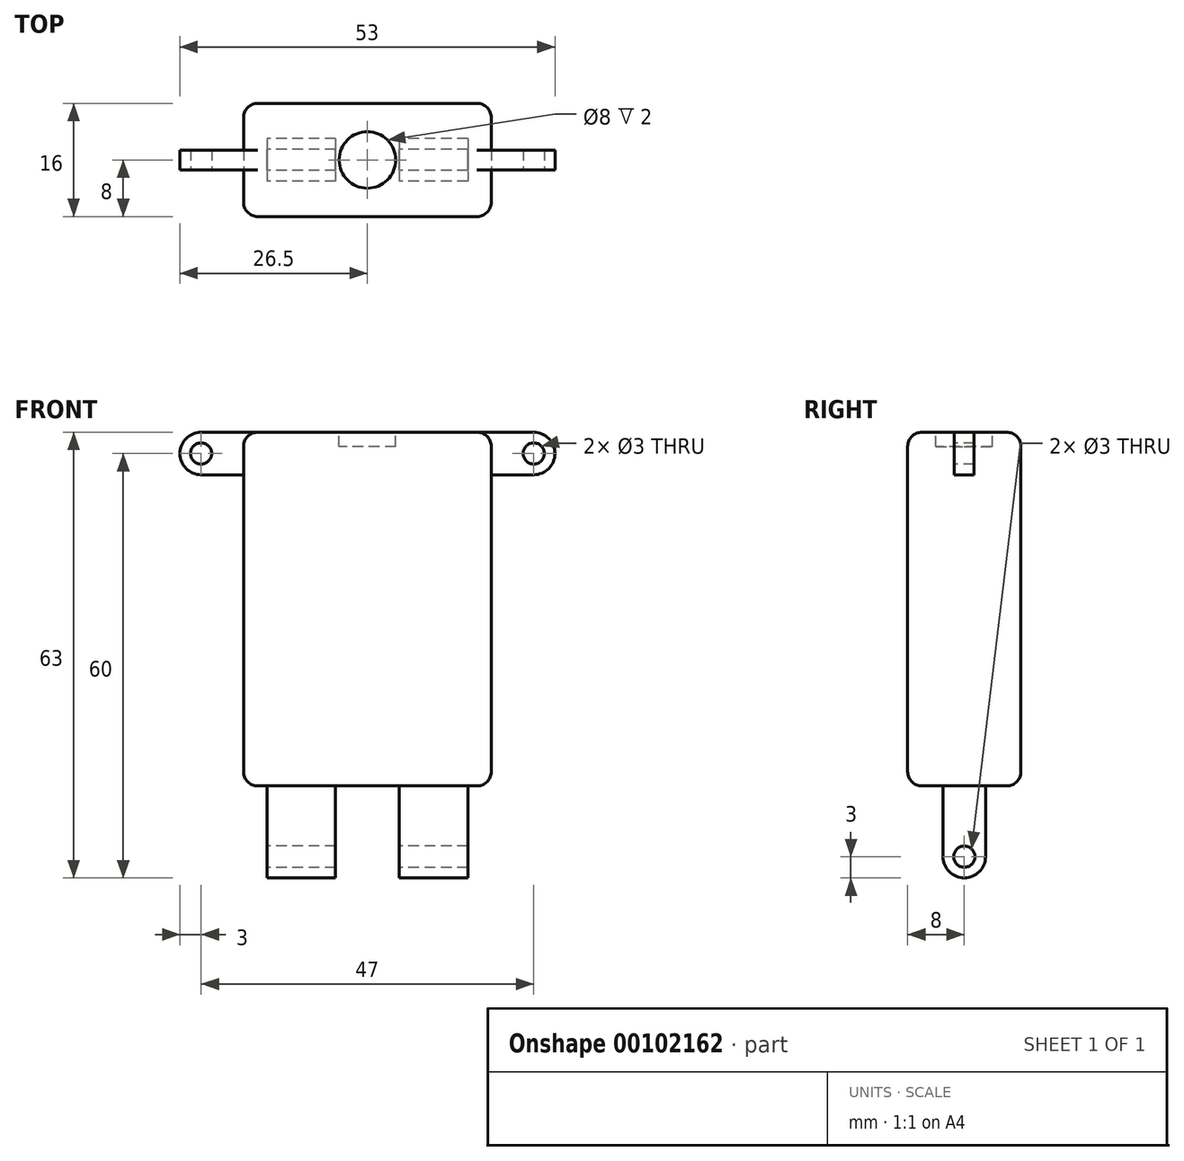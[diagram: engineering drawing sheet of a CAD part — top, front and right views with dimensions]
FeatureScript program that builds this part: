
annotation { "Feature Type Name" : "Feature", "Feature Type Description" : "" }
export const myFeature = defineFeature(function(context is Context, id is Id, definition is map)
    precondition{}
    {
        {
            var Q0;
            Q0=qCreatedBy(makeId("Right.planeOp"),FACE);
            var sketch = newSketch(context, id + "F0", { "sketchPlane" : qUnion([Q0])});
            skLineSegment(sketch, "E0.bottom", {"start": v(8, 0) * mm, "end": v(-8, 0) * mm});
            skLineSegment(sketch, "E0.top", {"start": v(8, 50) * mm, "end": v(-8, 50) * mm});
            skLineSegment(sketch, "E0.left", {"start": v(8, 0) * mm, "end": v(8, 50) * mm});
            skLineSegment(sketch, "E0.right", {"start": v(-8, 0) * mm, "end": v(-8, 50) * mm});
            skLineSegment(sketch, "E1.bottom", {"start": v(-3, 0) * mm, "end": v(3, 0) * mm});
            skLineSegment(sketch, "E1.top", {"start": v(-1.5, -10) * mm, "end": v(1.5, -10) * mm});
            skLineSegment(sketch, "E1.left", {"start": v(-3, 0) * mm, "end": v(-3, -10) * mm});
            skLineSegment(sketch, "E1.right", {"start": v(3, 0) * mm, "end": v(3, -10) * mm});
            skCircle(sketch, "E2", {"center": v(0, -10) * mm, "radius": 3 * mm});
            skCircle(sketch, "E3", {"center": v(0, -10) * mm, "radius": 1.5 * mm});
            skSolve(sketch);
        }
        {
            var Q0;
            Q0 = qSketchRegion(id + "F0", true);
            extrude(context, id + "F1", {"entities" : qUnion([Q0]), "depth" : 35 * mm, "symmetric" : true});
        }
        {
            var Q0;
            Q0=qCreatedBy(makeId("Front.planeOp"),FACE);
            var sketch = newSketch(context, id + "F2", { "sketchPlane" : qUnion([Q0])});
            skLineSegment(sketch, "E4.bottom", {"start": v(-14.2, 0) * mm, "end": v(-4.5, 0) * mm, "construction": true});
            skLineSegment(sketch, "E4.top", {"start": v(-14.2, -15) * mm, "end": v(-4.5, -15) * mm, "construction": true});
            skLineSegment(sketch, "E4.left", {"start": v(-14.2, 0) * mm, "end": v(-14.2, -15) * mm, "construction": true});
            skLineSegment(sketch, "E4.right", {"start": v(-4.5, 0) * mm, "end": v(-4.5, -15) * mm, "construction": true});
            skLineSegment(sketch, "E5.bottom", {"start": v(-14.2, 0) * mm, "end": v(-20.57, 0) * mm});
            skLineSegment(sketch, "E5.top", {"start": v(-14.2, -17.87) * mm, "end": v(-20.57, -17.87) * mm});
            skLineSegment(sketch, "E5.left", {"start": v(-14.2, 0) * mm, "end": v(-14.2, -17.87) * mm});
            skLineSegment(sketch, "E5.right", {"start": v(-20.57, 0) * mm, "end": v(-20.57, -17.87) * mm});
            skLineSegment(sketch, "E6.bottom", {"start": v(-4.5, 0) * mm, "end": v(0, 0) * mm});
            skLineSegment(sketch, "E6.top", {"start": v(-4.5, -17.87) * mm, "end": v(0, -17.87) * mm});
            skLineSegment(sketch, "E6.left", {"start": v(-4.5, 0) * mm, "end": v(-4.5, -17.87) * mm});
            skLineSegment(sketch, "E6.right", {"start": v(0, 0) * mm, "end": v(0, -17.87) * mm});
            skLineSegment(sketch, "E7.MirrorCS", {"start": v(4.5, 0) * mm, "end": v(4.5, -15) * mm, "construction": true});
            skLineSegment(sketch, "E8.MirrorCS", {"start": v(14.2, 0) * mm, "end": v(14.2, -15) * mm, "construction": true});
            skLineSegment(sketch, "E9.MirrorCS", {"start": v(4.5, 0) * mm, "end": v(4.5, -17.87) * mm});
            skLineSegment(sketch, "E10.MirrorCS", {"start": v(4.5, -17.87) * mm, "end": v(0, -17.87) * mm});
            skLineSegment(sketch, "E11.MirrorCS", {"start": v(4.5, 0) * mm, "end": v(0, 0) * mm});
            skLineSegment(sketch, "E12.MirrorCS", {"start": v(14.2, 0) * mm, "end": v(14.2, -17.87) * mm});
            skLineSegment(sketch, "E13.MirrorCS", {"start": v(14.2, -17.87) * mm, "end": v(20.57, -17.87) * mm});
            skLineSegment(sketch, "E14.MirrorCS", {"start": v(14.2, 0) * mm, "end": v(20.57, 0) * mm});
            skLineSegment(sketch, "E15.MirrorCS", {"start": v(20.57, 0) * mm, "end": v(20.57, -17.87) * mm});
            skLineSegment(sketch, "E16.MirrorCS", {"start": v(14.2, -15) * mm, "end": v(4.5, -15) * mm, "construction": true});
            skLineSegment(sketch, "E17.MirrorCS", {"start": v(14.2, 0) * mm, "end": v(4.5, 0) * mm, "construction": true});
            skSolve(sketch);
        }
        {
            var Q0;
            Q0 = qSketchRegion(id + "F2", true);
            extrude(context, id + "F3", {"entities" : qUnion([Q0]), "operationType" : NewBodyOperationType.REMOVE, "oppositeDirection" : true, "depth" : 25 * mm, "symmetric" : true});
        }
        {
            var Q0;
            Q0=makeQuery(id+"F1.opExtrude","SWEPT_FACE",FACE,{"disambiguationData":[OSD([sQuery(id+"F0.wireOp",EDGE,"E0.top")])]});
            cPlane(context, id + "F4", {"entities" : qUnion([Q0]), "cplaneType" : CPlaneType.OFFSET, "offset" : 0 * mm, "width" : 150 * mm, "height" : 150 * mm});
        }
        {
            var Q0;
            Q0=qCreatedBy(id+"F4.planeOp",FACE);
            var sketch = newSketch(context, id + "F5", { "sketchPlane" : qUnion([Q0])});
            skCircle(sketch, "E18", {"center": v(0, 0) * mm, "radius": 4 * mm});
            skSolve(sketch);
        }
        {
            var Q0;
            Q0=makeQuery(id+"F5.imprint","IMPRINT",FACE,{"disambiguationData":[TD([[makeQuery(id+"F5.imprint","IMPRINT",EDGE,{"derivedFrom":sQuery(id+"F5.wireOp",EDGE,"E18")}),1.0]])]});
            extrude(context, id + "F6", {"entities" : qUnion([Q0]), "operationType" : NewBodyOperationType.REMOVE, "oppositeDirection" : true, "depth" : 2 * mm});
        }
        {
            var Q0;
            Q0=qCreatedBy(makeId("Front.planeOp"),FACE);
            var sketch = newSketch(context, id + "F7", { "sketchPlane" : qUnion([Q0])});
            skLineSegment(sketch, "E19", {"start": v(17.5, 50) * mm, "end": v(23.5, 50) * mm});
            skArc(sketch, "E20", {"start": v(23.5, 50) * mm, "mid": v(26.5, 47) * mm, "end": v(23.5, 44) * mm});
            skLineSegment(sketch, "E21", {"start": v(23.5, 44) * mm, "end": v(17.5, 44) * mm});
            skLineSegment(sketch, "E22", {"start": v(17.5, 44) * mm, "end": v(17.5, 50) * mm});
            skCircle(sketch, "E23", {"center": v(23.5, 47) * mm, "radius": 1.5 * mm});
            skSolve(sketch);
        }
        {
            var Q0;
            Q0=makeQuery(id+"F7.imprint","IMPRINT",FACE,{"disambiguationData":[TD([[makeQuery(id+"F7.imprint","IMPRINT",EDGE,{"derivedFrom":sQuery(id+"F7.wireOp",EDGE,"E19")}),-1.0]])]});
            extrude(context, id + "F8", {"entities" : qUnion([Q0]), "oppositeDirection" : true, "depth" : 2.8 * mm, "symmetric" : true});
        }
        {
            var Q0;
            Q0=makeQuery(id+"F8.opExtrude","SWEPT_BODY",BODY,{"disambiguationData":[OSD([sQuery(id+"F7.wireOp",EDGE,"E19"),sQuery(id+"F7.wireOp",EDGE,"E20"),sQuery(id+"F7.wireOp",EDGE,"E21"),sQuery(id+"F7.wireOp",EDGE,"E22"),sQuery(id+"F7.wireOp",EDGE,"E23")])]});
            var Q1;
            Q1=qCreatedBy(makeId("Right.planeOp"),FACE);
            mirror(context, id + "F9", {"operationType" : NewBodyOperationType.ADD, "entities" : qUnion([Q0]), "mirrorPlane" : qUnion([Q1])});
        }
        {
            var Q0;
            Q0=makeQuery(id+"F1.opExtrude","SWEPT_FACE",FACE,{"disambiguationData":[OSD([sQuery(id+"F0.wireOp",EDGE,"E0.right")])]});
            var Q1;
            Q1=makeQuery(id+"F1.opExtrude","SWEPT_FACE",FACE,{"disambiguationData":[OSD([sQuery(id+"F0.wireOp",EDGE,"E0.left")])]});
            fillet(context, id + "F10", {"entities" : qUnion([Q0, Q1]), "radius" : 2 * mm, "tangentPropagation" : true, "allowEdgeOverflow" : false});
        }
        {
            var Q0;
            Q0=makeQuery(id+"F1.opExtrude","CAP_EDGE",EDGE,{"disambiguationData":[OSD([sQuery(id+"F0.wireOp",EDGE,"E0.right")])],"isStart":true});
            var Q1;
            Q1=makeQuery(id+"F1.opExtrude","CAP_EDGE",EDGE,{"disambiguationData":[OSD([sQuery(id+"F0.wireOp",EDGE,"E0.left")])],"isStart":true});
            var Q2;
            Q2=makeQuery(id+"F1.opExtrude","CAP_EDGE",EDGE,{"disambiguationData":[OSD([sQuery(id+"F0.wireOp",EDGE,"E0.right")])],"isStart":false});
            var Q3;
            Q3=makeQuery(id+"F1.opExtrude","CAP_EDGE",EDGE,{"disambiguationData":[OSD([sQuery(id+"F0.wireOp",EDGE,"E0.left")])],"isStart":false});
            var Q4;
            Q4=makeQuery(id+"F1.opExtrude","SWEPT_EDGE",EDGE,{"disambiguationData":[OSD([sQuery(id+"F0.wireOp",EDGE,"E0.top"),sQuery(id+"F0.wireOp",EDGE,"E0.right")])]});
            var Q5;
            Q5=makeQuery(id+"F1.opExtrude","SWEPT_EDGE",EDGE,{"disambiguationData":[OSD([sQuery(id+"F0.wireOp",EDGE,"E0.top"),sQuery(id+"F0.wireOp",EDGE,"E0.left")])]});
            var Q6;
            Q6=makeQuery(id+"F3.boolean.opBoolean","INTERSECT",EDGE,{"disambiguationData":[OD(1.0)],"derivedFrom":[makeQuery(id+"F3.opExtrude","SWEPT_FACE",FACE,{"disambiguationData":[OSD([sQuery(id+"F2.wireOp",EDGE,"E5.bottom")])]}),makeQuery(id+"F3.opExtrude","SWEPT_FACE",FACE,{"disambiguationData":[OSD([sQuery(id+"F2.wireOp",EDGE,"E6.bottom"),sQuery(id+"F2.wireOp",EDGE,"E11.MirrorCS")])]}),makeQuery(id+"F3.opExtrude","SWEPT_FACE",FACE,{"disambiguationData":[OSD([sQuery(id+"F2.wireOp",EDGE,"E14.MirrorCS")])]})]});
            var Q7;
            {var subQ0=sQuery(id+"F0.wireOp",EDGE,"E0.bottom");Q7=makeQuery(id+"F3.boolean.opBoolean","MERGE",EDGE,{"derivedFrom":[makeQuery(id+"F1.opExtrude","CAP_EDGE",EDGE,{"disambiguationData":[OSD([subQ0]),TDD([makeQuery(id+"F0.imprint","IMPRINT",EDGE,{"disambiguationData":[TD([[makeQuery(id+"F0.imprint","INTERSECT",VERTEX,{"derivedFrom":[subQ0,sQuery(id+"F0.wireOp",EDGE,"E0.left")]}),-1.0]])],"derivedFrom":subQ0})])],"isStart":true}),makeQuery(id+"F1.opExtrude","CAP_EDGE",EDGE,{"disambiguationData":[OSD([subQ0]),TDD([makeQuery(id+"F0.imprint","IMPRINT",EDGE,{"disambiguationData":[TD([[makeQuery(id+"F0.imprint","INTERSECT",VERTEX,{"derivedFrom":[subQ0,sQuery(id+"F0.wireOp",EDGE,"E0.right")]}),1.0]])],"derivedFrom":subQ0})])],"isStart":true})]});}
            var Q8;
            {var subQ0=sQuery(id+"F0.wireOp",EDGE,"E0.bottom");Q8=makeQuery(id+"F3.boolean.opBoolean","MERGE",EDGE,{"derivedFrom":[makeQuery(id+"F1.opExtrude","CAP_EDGE",EDGE,{"disambiguationData":[OSD([subQ0]),TDD([makeQuery(id+"F0.imprint","IMPRINT",EDGE,{"disambiguationData":[TD([[makeQuery(id+"F0.imprint","INTERSECT",VERTEX,{"derivedFrom":[subQ0,sQuery(id+"F0.wireOp",EDGE,"E0.left")]}),-1.0]])],"derivedFrom":subQ0})])],"isStart":false}),makeQuery(id+"F1.opExtrude","CAP_EDGE",EDGE,{"disambiguationData":[OSD([subQ0]),TDD([makeQuery(id+"F0.imprint","IMPRINT",EDGE,{"disambiguationData":[TD([[makeQuery(id+"F0.imprint","INTERSECT",VERTEX,{"derivedFrom":[subQ0,sQuery(id+"F0.wireOp",EDGE,"E0.right")]}),1.0]])],"derivedFrom":subQ0})])],"isStart":false})]});}
            var Q9;
            Q9=makeQuery(id+"F3.boolean.opBoolean","INTERSECT",EDGE,{"disambiguationData":[OD(0.0)],"derivedFrom":[makeQuery(id+"F3.opExtrude","SWEPT_FACE",FACE,{"disambiguationData":[OSD([sQuery(id+"F2.wireOp",EDGE,"E5.bottom")])]}),makeQuery(id+"F3.opExtrude","SWEPT_FACE",FACE,{"disambiguationData":[OSD([sQuery(id+"F2.wireOp",EDGE,"E6.bottom"),sQuery(id+"F2.wireOp",EDGE,"E11.MirrorCS")])]}),makeQuery(id+"F3.opExtrude","SWEPT_FACE",FACE,{"disambiguationData":[OSD([sQuery(id+"F2.wireOp",EDGE,"E14.MirrorCS")])]})]});
            var Q10;
            {var subQ0=sQuery(id+"F0.wireOp",EDGE,"E0.left");var subQ2=sQuery(id+"F0.wireOp",EDGE,"E0.top");Q10=makeQuery(id+"F9.boolean.opBoolean","SPLIT",EDGE,{"disambiguationData":[TD([makeQuery(id+"F1.opExtrude","SWEPT_FACE",FACE,{"disambiguationData":[OSD([subQ0])]})])],"derivedFrom":makeQuery(id+"F1.opExtrude","CAP_EDGE",EDGE,{"disambiguationData":[OSD([subQ2])],"isStart":false})});}
            var Q11;
            {var subQ0=sQuery(id+"F0.wireOp",EDGE,"E0.right");var subQ1=sQuery(id+"F0.wireOp",EDGE,"E0.top");Q11=makeQuery(id+"F9.boolean.opBoolean","SPLIT",EDGE,{"disambiguationData":[TD([makeQuery(id+"F1.opExtrude","SWEPT_FACE",FACE,{"disambiguationData":[OSD([subQ0])]})])],"derivedFrom":makeQuery(id+"F1.opExtrude","CAP_EDGE",EDGE,{"disambiguationData":[OSD([subQ1])],"isStart":false})});}
            var Q12;
            {var subQ2=sQuery(id+"F0.wireOp",EDGE,"E0.right");var subQ3=sQuery(id+"F0.wireOp",EDGE,"E0.top");Q12=makeQuery(id+"F9.boolean.opBoolean","SPLIT",EDGE,{"disambiguationData":[TD([makeQuery(id+"F1.opExtrude","SWEPT_FACE",FACE,{"disambiguationData":[OSD([subQ2])]})])],"derivedFrom":makeQuery(id+"F1.opExtrude","CAP_EDGE",EDGE,{"disambiguationData":[OSD([subQ3])],"isStart":true})});}
            var Q13;
            {var subQ2=sQuery(id+"F0.wireOp",EDGE,"E0.left");var subQ3=sQuery(id+"F0.wireOp",EDGE,"E0.top");Q13=makeQuery(id+"F9.boolean.opBoolean","SPLIT",EDGE,{"disambiguationData":[TD([makeQuery(id+"F1.opExtrude","SWEPT_FACE",FACE,{"disambiguationData":[OSD([subQ2])]})])],"derivedFrom":makeQuery(id+"F1.opExtrude","CAP_EDGE",EDGE,{"disambiguationData":[OSD([subQ3])],"isStart":true})});}
            fillet(context, id + "F11", {"entities" : qUnion([Q0, Q1, Q2, Q3, Q4, Q5, Q6, Q7, Q8, Q9, Q10, Q11, Q12, Q13]), "radius" : 2 * mm, "tangentPropagation" : true, "allowEdgeOverflow" : false});
        }
    });
